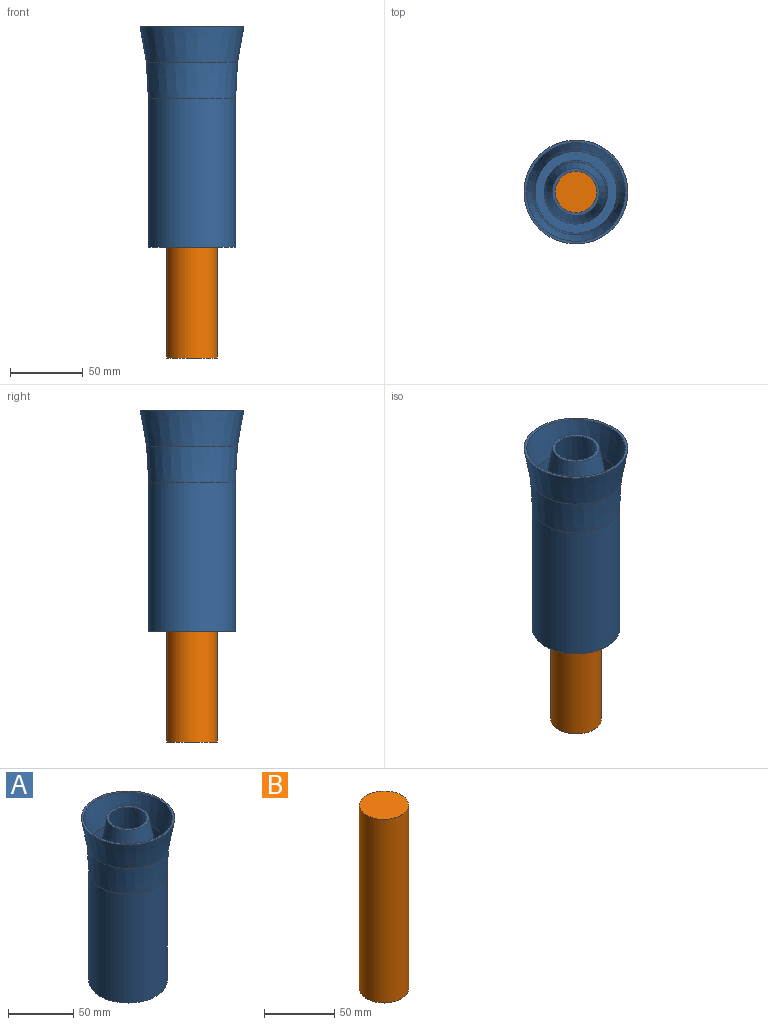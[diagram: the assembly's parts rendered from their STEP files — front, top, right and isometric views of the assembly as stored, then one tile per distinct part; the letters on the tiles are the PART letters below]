
ASSEMBLY  parts=2 mates=1
PART A: 16 faces, bbox 71.4x71.4x152 mm
  f0: plane 32.22x32.22mm, normal (0,0,1), area 174.5mm2, adj f3,f11
  f1: cone r=20mm half-angle=3deg, axis (0,0,-1), area 3042.9mm2, adj f3,f6
  f2: cone r=30mm half-angle=3deg, axis (0,0,1), area 4821.9mm2, adj f4,f7
  f3: cone r=18.69mm half-angle=10deg, axis (0,0,-1), area 2629.5mm2, adj f0,f1
  f4: cone r=31.31mm half-angle=10deg, axis (0,0,1), area 5345.6mm2, adj f2,f5
  f5: plane 71.44x71.44mm, normal (0,0,1), area 399.7mm2, adj f4,f12
  f6: cylinder r=20mm len=102mm, axis (0,0,1), area 12817.7mm2, adj f1,f8
  f7: cylinder r=30mm len=102mm, axis (0,0,1), area 19226.5mm2, adj f2,f8
  f8: plane 60x60mm, normal (0,0,-1), area 1570.8mm2, adj f6,f7
  f9: cone r=21.8mm half-angle=3deg, axis (0,0,-1), area 3346.2mm2, adj f11,f13
  f10: cone r=28.2mm half-angle=3deg, axis (0,0,1), area 4567.9mm2, adj f12,f14
  f11: cone r=20.46mm half-angle=10deg, axis (0,0,-1), area 2894.4mm2, adj f0,f9
  f12: cone r=29.54mm half-angle=10deg, axis (0,0,1), area 5015.7mm2, adj f5,f10
  f13: cylinder r=21.8mm len=100.25mm, axis (0,0,1), area 13731.2mm2, adj f9,f15
  f14: cylinder r=28.2mm len=100.25mm, axis (0,0,1), area 17762.4mm2, adj f10,f15
  f15: plane 56.4x56.4mm, normal (0,0,1), area 1005.3mm2, adj f13,f14
PART B: 3 faces, bbox 35x35x160 mm
  f0: cylinder r=17.5mm len=160mm, axis (0,0,1), area 17592.9mm2, adj f1,f2
  f1: plane 35x35mm, normal (0,0,1), area 962.1mm2, adj f0
  f2: plane 35x35mm, normal (0,0,-1), area 962.1mm2, adj f0
PLACE A rot(axis=(0,0,1),0deg) t=(-0.66,-2.97,17.78)mm
PLACE B t=(-0.66,-2.97,-12.91)mm
MATE cylindrical A.f1 <-> B.f0  axis (0,0,-1) through (-0.66,-2.97,30.28)mm
